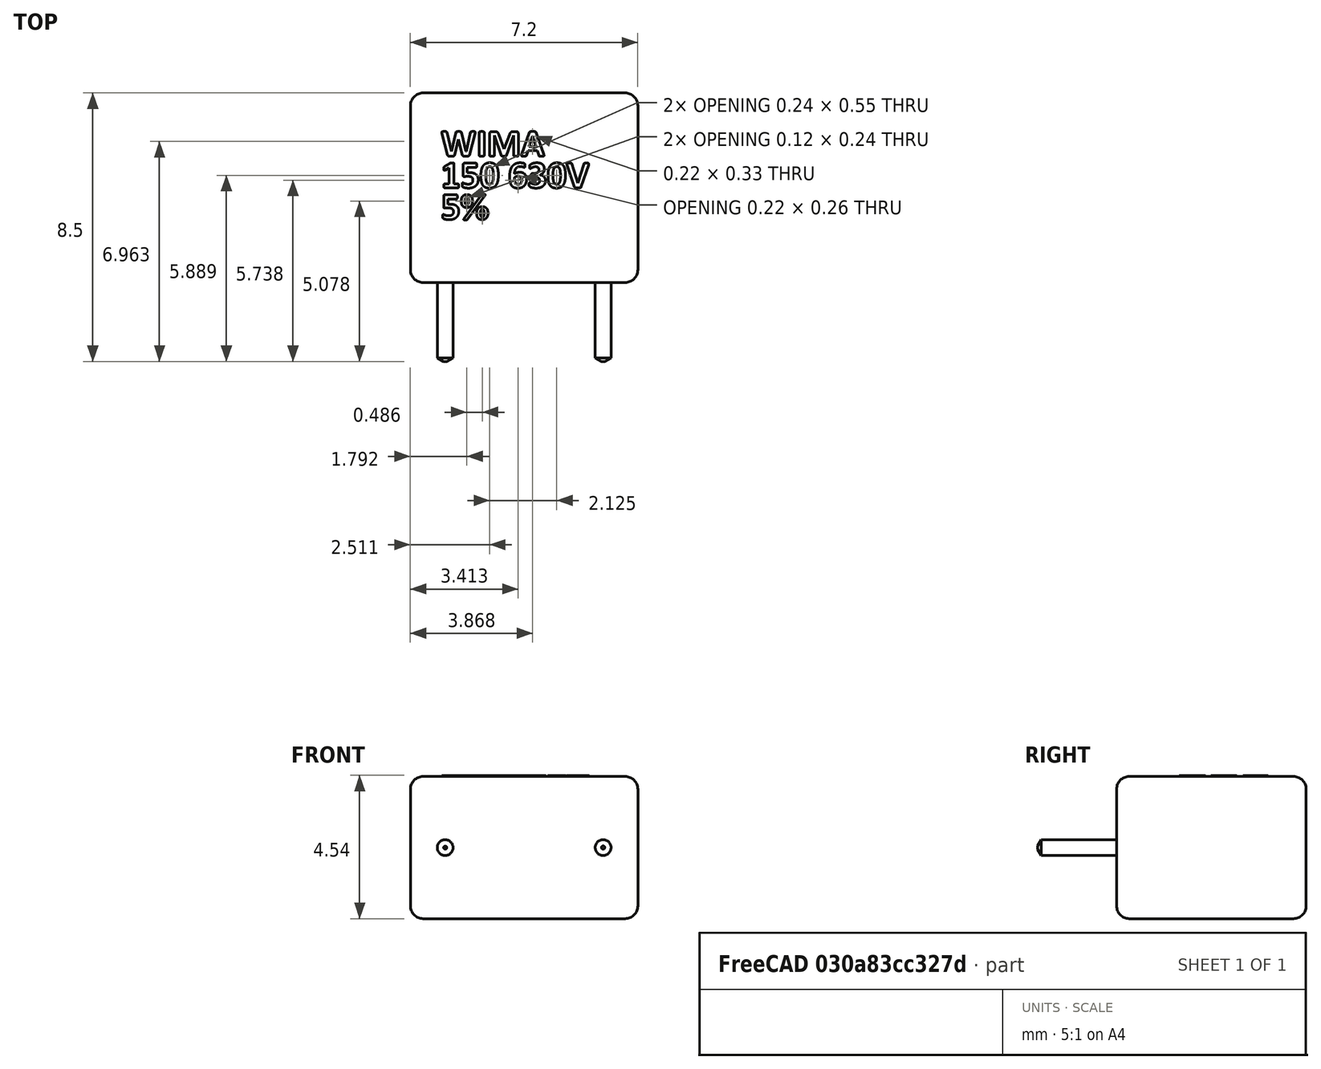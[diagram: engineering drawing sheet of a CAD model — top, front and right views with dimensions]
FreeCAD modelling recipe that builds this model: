
FCSTD DOCUMENT  (FreeCAD 0.17R13528 (Git))
Label: WIMA_pF
License: All rights reserved
LicenseURL: http://en.wikipedia.org/wiki/All_rights_reserved
objects: Part::Part2DObjectPython×3, Part::Extrusion×3, Part::Feature×1, Part::Fuse×1, Part::MultiFuse×1
note: 9 computed .brp shape members not serialized (recipe doc carries the construction recipe); baked Part::Feature solids carry a one-line shape summary decoded from their .brp

FEATURE [Part::Feature] Part__Feature  label="WIMA_D"
  shape: bbox 7.2 x 8.5 x 4.5 mm, 36 faces (baked)
FEATURE [Part::Part2DObjectPython] ShapeString  label="TextRow1"  # Draft 2D object (typed FeaturePython)
  FontFile = <userpath>/Desktop/Freecad Projects/calibrib.ttf
  Placement = pos=(-0.5,4,2.26) rot=(0,0,1;0rad)
  Size = 1
  String = WIMA
  Support = -> [Part__Feature]
  Tracking = 0
FEATURE [Part::Part2DObjectPython] ShapeString001  label="TextRow2"  # Draft 2D object (typed FeaturePython)
  FontFile = <userpath>/Desktop/Freecad Projects/calibrib.ttf
  Placement = pos=(-0.5,3,2.26) rot=(0,0,1;0rad)
  Size = 1
  String = 150 630V
  Support = -> [Part__Feature]
  Tracking = 0
FEATURE [Part::Part2DObjectPython] ShapeString002  label="TextRow3"  # Draft 2D object (typed FeaturePython)
  FontFile = <userpath>/Desktop/Freecad Projects/calibrib.ttf
  Placement = pos=(-0.5,2,2.26) rot=(0,0,1;0rad)
  Size = 1
  String = 5%
  Support = -> [Part__Feature]
  Tracking = 0
FEATURE [Part::Extrusion] Extrude
  Base = -> ShapeString
  Dir = (0,0,1)
  DirMode = 2
  FaceMakerClass = Part::FaceMakerBullseye
  LengthFwd = 0.025
  LengthRev = 0
  Solid = true
  Symmetric = false
FEATURE [Part::Extrusion] Extrude001
  Base = -> ShapeString001
  Dir = (0,0,1)
  DirMode = 2
  FaceMakerClass = Part::FaceMakerBullseye
  LengthFwd = 0.025
  LengthRev = 0
  Solid = true
  Symmetric = false
FEATURE [Part::Extrusion] Extrude002
  Base = -> ShapeString002
  Dir = (0,0,1)
  DirMode = 2
  FaceMakerClass = Part::FaceMakerBullseye
  LengthFwd = 0.025
  LengthRev = 0
  Solid = true
  Symmetric = false
FEATURE [Part::Fuse] Fusion
  Base = -> Part__Feature
  Tool = -> Extrude
FEATURE [Part::MultiFuse] Fusion001
  Shapes = -> [Fusion,Extrude001,Extrude002]
